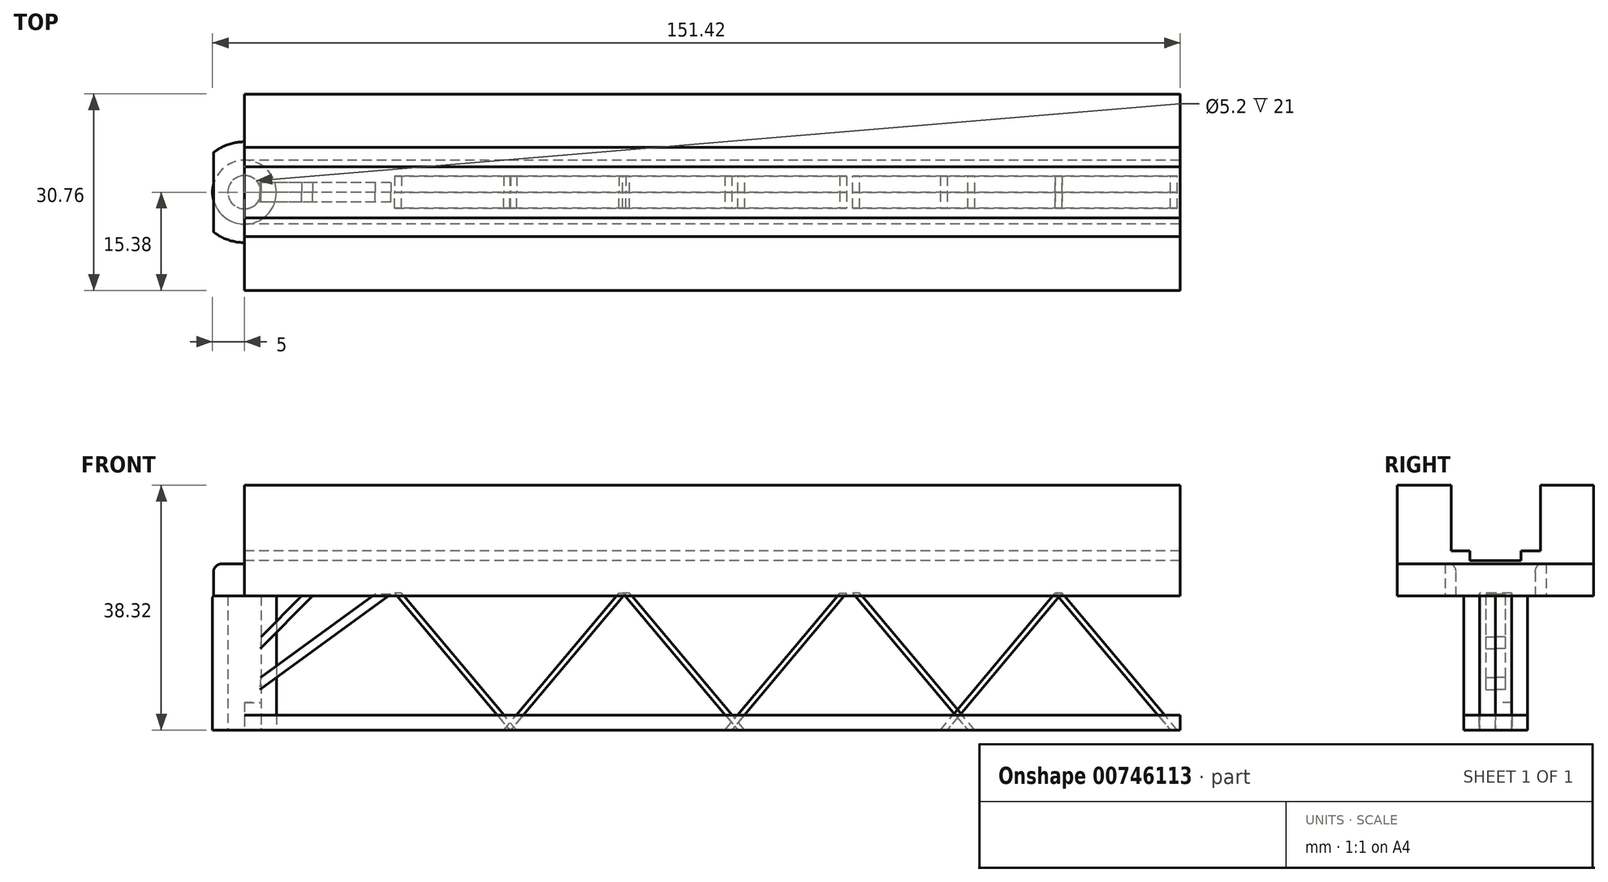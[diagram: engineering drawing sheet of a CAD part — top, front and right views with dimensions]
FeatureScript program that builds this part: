
annotation { "Feature Type Name" : "Feature", "Feature Type Description" : "" }
export const myFeature = defineFeature(function(context is Context, id is Id, definition is map)
    precondition{}
    {
        {
            var Q0;
            Q0=qCreatedBy(makeId("Top.planeOp"),FACE);
            var sketch = newSketch(context, id + "F0", { "sketchPlane" : qUnion([Q0])});
            skCircle(sketch, "E0", {"center": v(0, 0) * mm, "radius": 2.6 * mm});
            skSolve(sketch);
        }
        {
            var Q0;
            Q0=qCreatedBy(makeId("Top.planeOp"),FACE);
            var sketch = newSketch(context, id + "F1", { "sketchPlane" : qUnion([Q0])});
            skCircle(sketch, "E1", {"center": v(0, 0) * mm, "radius": 5 * mm});
            skSolve(sketch);
        }
        {
            var Q0;
            Q0=makeQuery(id+"F1.imprint","IMPRINT",FACE,{"disambiguationData":[TD([[makeQuery(id+"F1.imprint","IMPRINT",EDGE,{"derivedFrom":sQuery(id+"F1.wireOp",EDGE,"E1")}),1.0]])]});
            extrude(context, id + "F2", {"entities" : qUnion([Q0]), "depth" : 21 * mm, "offsetDistance" : 25.4 * mm});
        }
        {
            var Q0;
            Q0=makeQuery(id+"F0.imprint","IMPRINT",FACE,{"disambiguationData":[TD([[makeQuery(id+"F0.imprint","IMPRINT",EDGE,{"derivedFrom":sQuery(id+"F0.wireOp",EDGE,"E0")}),1.0]])]});
            extrude(context, id + "F3", {"entities" : qUnion([Q0]), "operationType" : NewBodyOperationType.REMOVE, "depth" : 22.53 * mm, "offsetDistance" : 25.4 * mm});
        }
        {
            var Q0;
            Q0=qCreatedBy(makeId("Front.planeOp"),FACE);
            var sketch = newSketch(context, id + "F4", { "sketchPlane" : qUnion([Q0])});
            skLineSegment(sketch, "E2", {"start": v(-4.85, 21) * mm, "end": v(-4.85, 24.75) * mm});
            skLineSegment(sketch, "E3", {"start": v(-3.58, 26.02) * mm, "end": v(146.42, 26.02) * mm});
            skLineSegment(sketch, "E4", {"start": v(146.42, 26.02) * mm, "end": v(146.42, 21) * mm});
            skLineSegment(sketch, "E5", {"start": v(146.42, 21) * mm, "end": v(3, 21) * mm});
            skPoint(sketch, "E6.visualSharp", {"position": v(-4.85, 26.02) * mm});
            skArc(sketch, "E6.filletArc", {"start": v(-3.58, 26.02) * mm, "mid": v(-4.48, 25.65) * mm, "end": v(-4.85, 24.75) * mm});
            skLineSegment(sketch, "E7", {"start": v(3, 21) * mm, "end": v(-4.85, 21) * mm});
            skSolve(sketch);
        }
        {
            var Q0;
            Q0=makeQuery(id+"F4.imprint","IMPRINT",FACE,{"disambiguationData":[TD([[makeQuery(id+"F4.imprint","IMPRINT",EDGE,{"derivedFrom":sQuery(id+"F4.wireOp",EDGE,"E2")}),-1.0]])]});
            extrude(context, id + "F5", {"entities" : qUnion([Q0]), "depth" : 22.86 * mm, "offsetDistance" : 25.4 * mm});
        }
        {
            var Q0;
            Q0=makeQuery(id+"F5.opExtrude","CAP_FACE",FACE,{"disambiguationData":[OSD([sQuery(id+"F4.wireOp",EDGE,"E2"),sQuery(id+"F4.wireOp",EDGE,"E3"),sQuery(id+"F4.wireOp",EDGE,"E4"),sQuery(id+"F4.wireOp",EDGE,"E5"),sQuery(id+"F4.wireOp",EDGE,"E6.filletArc"),sQuery(id+"F4.wireOp",EDGE,"E7")])],"isStart":true});
            extrude(context, id + "F6", {"entities" : qUnion([Q0]), "operationType" : NewBodyOperationType.ADD, "depth" : 22.86 * mm, "offsetDistance" : 25.4 * mm});
        }
        {
            var Q0;
            {var subQ0=sQuery(id+"F4.wireOp",EDGE,"E3");Q0=makeQuery(id+"F6.boolean.opBoolean","MERGE",FACE,{"derivedFrom":[makeQuery(id+"F5.opExtrude","SWEPT_FACE",FACE,{"disambiguationData":[OSD([subQ0])]}),makeQuery(id+"F6.opExtrude","SWEPT_FACE",FACE,{"disambiguationData":[OSD([subQ0])]})]});}
            var sketch = newSketch(context, id + "F7", { "sketchPlane" : qUnion([Q0])});
            skLineSegment(sketch, "E8.bottom", {"start": v(73.66, -10.5) * mm, "end": v(94.66, -10.5) * mm});
            skLineSegment(sketch, "E8.top", {"start": v(73.66, 10.5) * mm, "end": v(94.66, 10.5) * mm});
            skLineSegment(sketch, "E8.left", {"start": v(73.66, -10.5) * mm, "end": v(73.66, 10.5) * mm});
            skLineSegment(sketch, "E8.right", {"start": v(94.66, -10.5) * mm, "end": v(94.66, 10.5) * mm});
            skPoint(sketch, "E8.middle", {"position": v(84.16, 0) * mm});
            skSolve(sketch);
        }
        {
            var Q0;
            {var subQ0=sQuery(id+"F4.wireOp",EDGE,"E7");var subQ1=sQuery(id+"F4.wireOp",EDGE,"E5");Q0=makeQuery(id+"F6.boolean.opBoolean","MERGE",FACE,{"derivedFrom":[makeQuery(id+"F5.opExtrude","SWEPT_FACE",FACE,{"disambiguationData":[OSD([subQ1,subQ0])]}),makeQuery(id+"F6.opExtrude","SWEPT_FACE",FACE,{"disambiguationData":[OSD([subQ1,subQ0])]})]});}
            var sketch = newSketch(context, id + "F8", { "sketchPlane" : qUnion([Q0])});
            skLineSegment(sketch, "E9", {"start": v(-4.85, -22.86) * mm, "end": v(-4.85, 22.86) * mm});
            skArc(sketch, "E10", {"start": v(0, 7.9) * mm, "mid": v(-7.9, 0) * mm, "end": v(0, -7.9) * mm});
            skLineSegment(sketch, "E11", {"start": v(0, -22.86) * mm, "end": v(0, -7.9) * mm});
            skLineSegment(sketch, "E12", {"start": v(-4.85, 22.86) * mm, "end": v(0, 22.86) * mm});
            skLineSegment(sketch, "E13", {"start": v(0, 22.86) * mm, "end": v(0, 7.9) * mm});
            skLineSegment(sketch, "E14", {"start": v(-4.85, -22.86) * mm, "end": v(0, -22.86) * mm});
            skLineSegment(sketch, "E15", {"start": v(10.56, -22.86) * mm, "end": v(10.56, 22.86) * mm});
            skSolve(sketch);
        }
        {
            var Q0;
            Q0=qSketchRegion(id+"F8",true);
            extrude(context, id + "F9", {"entities" : qUnion([Q0]), "operationType" : NewBodyOperationType.REMOVE, "oppositeDirection" : true, "depth" : 25.4 * mm, "offsetDistance" : 25.4 * mm});
        }
        {
            var Q0;
            Q0=makeQuery(id+"FSWrnr269RCgbZk_2.boolean.opBoolean","SPLIT",EDGE,{"derivedFrom":makeQuery(id+"F2.opExtrude","CAP_EDGE",EDGE,{"disambiguationData":[OSD([sQuery(id+"F1.wireOp",EDGE,"E1")])],"isStart":false})});
            fillet(context, id + "F10", {"entities" : qUnion([Q0]), "radius" : 0.3 * mm, "tangentPropagation" : true, "allowEdgeOverflow" : false});
        }
        {
            var Q0;
            Q0=qCreatedBy(makeId("Front.planeOp"),FACE);
            var sketch = newSketch(context, id + "F11", { "sketchPlane" : qUnion([Q0])});
            skLineSegment(sketch, "E16", {"start": v(10.69, 21.02) * mm, "end": v(2.5, 12.74) * mm});
            skLineSegment(sketch, "E17", {"start": v(10.69, 21.02) * mm, "end": v(8.95, 21.02) * mm});
            skLineSegment(sketch, "E18", {"start": v(8.95, 21.02) * mm, "end": v(2.59, 14.59) * mm});
            skLineSegment(sketch, "E19", {"start": v(2.59, 14.59) * mm, "end": v(2.5, 12.74) * mm});
            skSolve(sketch);
        }
        {
            var Q0;
            Q0=makeQuery(id+"F11.imprint","IMPRINT",FACE,{"disambiguationData":[TD([[makeQuery(id+"F11.imprint","IMPRINT",EDGE,{"derivedFrom":sQuery(id+"F11.wireOp",EDGE,"E16")}),-1.0]])]});
            extrude(context, id + "F12", {"entities" : qUnion([Q0]), "depth" : 1.52 * mm, "offsetDistance" : 25.4 * mm});
        }
        {
            var Q0;
            Q0=makeQuery(id+"F12.opExtrude","CAP_FACE",FACE,{"disambiguationData":[OSD([sQuery(id+"F11.wireOp",EDGE,"E16"),sQuery(id+"F11.wireOp",EDGE,"E17"),sQuery(id+"F11.wireOp",EDGE,"E18"),sQuery(id+"F11.wireOp",EDGE,"E19")])],"isStart":true});
            extrude(context, id + "F13", {"entities" : qUnion([Q0]), "depth" : 1.52 * mm, "offsetDistance" : 25.4 * mm});
        }
        {
            var Q0;
            Q0=qSketchRegion(id+"F7",true);
            extrude(context, id + "F14", {"entities" : qUnion([Q0]), "operationType" : NewBodyOperationType.REMOVE, "depth" : 12.95 * mm, "offsetDistance" : 25.4 * mm});
        }
        {
            var Q0;
            Q0=qCreatedBy(makeId("Front.planeOp"),FACE);
            var sketch = newSketch(context, id + "F15", { "sketchPlane" : qUnion([Q0])});
            skLineSegment(sketch, "E20", {"start": v(22.9, 21.28) * mm, "end": v(2.41, 6.35) * mm});
            skLineSegment(sketch, "E21", {"start": v(22.9, 21.28) * mm, "end": v(20.45, 21.28) * mm});
            skLineSegment(sketch, "E22", {"start": v(20.45, 21.28) * mm, "end": v(2.5, 8.2) * mm});
            skLineSegment(sketch, "E23", {"start": v(2.5, 8.2) * mm, "end": v(2.41, 6.35) * mm});
            skSolve(sketch);
        }
        {
            var Q0;
            Q0=makeQuery(id+"F15.imprint","IMPRINT",FACE,{"disambiguationData":[TD([[makeQuery(id+"F15.imprint","IMPRINT",EDGE,{"derivedFrom":sQuery(id+"F15.wireOp",EDGE,"E20")}),-1.0]])]});
            extrude(context, id + "F16", {"entities" : qUnion([Q0]), "depth" : 1.52 * mm, "offsetDistance" : 25.4 * mm});
        }
        {
            var Q0;
            Q0=qSketchRegion(id+"F15",true);
            extrude(context, id + "F17", {"entities" : qUnion([Q0]), "oppositeDirection" : true, "depth" : 1.52 * mm, "offsetDistance" : 25.4 * mm});
        }
        {
            var Q0;
            {var subQ0=sQuery(id+"F4.wireOp",EDGE,"E3");Q0=makeQuery(id+"F6.boolean.opBoolean","MERGE",FACE,{"derivedFrom":[makeQuery(id+"F5.opExtrude","SWEPT_FACE",FACE,{"disambiguationData":[OSD([subQ0])]}),makeQuery(id+"F6.opExtrude","SWEPT_FACE",FACE,{"disambiguationData":[OSD([subQ0])]})]});}
            var sketch = newSketch(context, id + "F18", { "sketchPlane" : qUnion([Q0])});
            skLineSegment(sketch, "E24", {"start": v(0, 15.38) * mm, "end": v(146.42, 15.38) * mm});
            skLineSegment(sketch, "E25", {"start": v(146.42, 15.38) * mm, "end": v(146.42, 22.86) * mm});
            skLineSegment(sketch, "E26", {"start": v(146.42, 22.86) * mm, "end": v(0, 22.86) * mm});
            skLineSegment(sketch, "E27", {"start": v(0, 22.86) * mm, "end": v(0, 15.38) * mm});
            skLineSegment(sketch, "E28", {"start": v(0, -15.38) * mm, "end": v(146.42, -15.38) * mm});
            skLineSegment(sketch, "E29", {"start": v(0, -15.38) * mm, "end": v(0, -22.86) * mm});
            skLineSegment(sketch, "E30", {"start": v(0, -22.86) * mm, "end": v(146.42, -22.86) * mm});
            skLineSegment(sketch, "E31", {"start": v(146.42, -22.86) * mm, "end": v(146.42, -15.38) * mm});
            skSolve(sketch);
        }
        {
            var Q0;
            Q0=qSketchRegion(id+"F18",true);
            extrude(context, id + "F19", {"entities" : qUnion([Q0]), "operationType" : NewBodyOperationType.REMOVE, "oppositeDirection" : true, "depth" : 25.4 * mm, "offsetDistance" : 25.4 * mm});
        }
        {
            var Q0;
            Q0=qCreatedBy(makeId("Right.planeOp"),FACE);
            var sketch = newSketch(context, id + "F20", { "sketchPlane" : qUnion([Q0])});
            skLineSegment(sketch, "E32.bottom", {"start": v(-5, 2.35) * mm, "end": v(4.99, 2.35) * mm});
            skLineSegment(sketch, "E32.top", {"start": v(-5, 0) * mm, "end": v(4.99, 0) * mm});
            skLineSegment(sketch, "E32.left", {"start": v(-5, 2.35) * mm, "end": v(-5, 0) * mm});
            skLineSegment(sketch, "E32.right", {"start": v(4.99, 2.35) * mm, "end": v(4.99, 0) * mm});
            skSolve(sketch);
        }
        {
            var Q0;
            Q0=qSketchRegion(id+"F20",true);
            extrude(context, id + "F21", {"entities" : qUnion([Q0]), "depth" : 146.42 * mm, "offsetDistance" : 25.4 * mm});
        }
        {
            var Q0;
            Q0=makeQuery(id+"F21.opExtrude","SWEPT_FACE",FACE,{"disambiguationData":[OSD([sQuery(id+"F20.wireOp",EDGE,"E32.top")])]});
            var sketch = newSketch(context, id + "F22", { "sketchPlane" : qUnion([Q0])});
            skArc(sketch, "E33", {"start": v(0, -2.62) * mm, "mid": v(2.6, 0) * mm, "end": v(0, 2.6) * mm});
            skLineSegment(sketch, "E34", {"start": v(0, 2.6) * mm, "end": v(0, -2.62) * mm});
            skSolve(sketch);
        }
        {
            var Q0;
            Q0=qSketchRegion(id+"F22",true);
            extrude(context, id + "F23", {"entities" : qUnion([Q0]), "operationType" : NewBodyOperationType.REMOVE, "oppositeDirection" : true, "depth" : 4.32 * mm, "offsetDistance" : 25 * mm});
        }
        {
            var Q0;
            Q0=qCreatedBy(makeId("Front.planeOp"),FACE);
            var sketch = newSketch(context, id + "F24", { "sketchPlane" : qUnion([Q0])});
            skLineSegment(sketch, "E35", {"start": v(23.5, 21.45) * mm, "end": v(41.5, 0) * mm});
            skLineSegment(sketch, "E36", {"start": v(41.5, 0) * mm, "end": v(42.58, 0) * mm});
            skLineSegment(sketch, "E37", {"start": v(42.58, 0) * mm, "end": v(24.57, 21.45) * mm});
            skLineSegment(sketch, "E38", {"start": v(24.57, 21.45) * mm, "end": v(23.5, 21.45) * mm});
            skSolve(sketch);
        }
        {
            var Q0;
            Q0=makeQuery(id+"F24.imprint","IMPRINT",FACE,{"disambiguationData":[TD([[makeQuery(id+"F24.imprint","IMPRINT",EDGE,{"derivedFrom":sQuery(id+"F24.wireOp",EDGE,"E35")}),1.0]])]});
            extrude(context, id + "F25", {"entities" : qUnion([Q0]), "depth" : 2.5 * mm, "offsetDistance" : 25 * mm});
        }
        {
            var Q0;
            Q0=qSketchRegion(id+"F24",true);
            extrude(context, id + "F26", {"entities" : qUnion([Q0]), "oppositeDirection" : true, "depth" : 2.5 * mm, "offsetDistance" : 25 * mm});
        }
        {
            var Q0;
            Q0=qCreatedBy(makeId("Front.planeOp"),FACE);
            var sketch = newSketch(context, id + "F27", { "sketchPlane" : qUnion([Q0])});
            skLineSegment(sketch, "E39.MirrorCS", {"start": v(41.65, 0) * mm, "end": v(40.57, 0) * mm});
            skLineSegment(sketch, "E40.MirrorCS", {"start": v(58.58, 21.45) * mm, "end": v(59.65, 21.45) * mm});
            skLineSegment(sketch, "E41.MirrorCS", {"start": v(59.65, 21.45) * mm, "end": v(41.65, 0) * mm});
            skLineSegment(sketch, "E42.MirrorCS", {"start": v(40.57, 0) * mm, "end": v(58.58, 21.45) * mm});
            skSolve(sketch);
        }
        {
            var Q0;
            Q0=makeQuery(id+"F27.imprint","IMPRINT",FACE,{"disambiguationData":[TD([[makeQuery(id+"F27.imprint","IMPRINT",EDGE,{"derivedFrom":sQuery(id+"F27.wireOp",EDGE,"E39.MirrorCS")}),-1.0]])]});
            extrude(context, id + "F28", {"entities" : qUnion([Q0]), "depth" : 2.5 * mm, "offsetDistance" : 25 * mm});
        }
        {
            var Q0;
            Q0=qSketchRegion(id+"F27",true);
            extrude(context, id + "F29", {"entities" : qUnion([Q0]), "oppositeDirection" : true, "depth" : 2.5 * mm, "offsetDistance" : 25 * mm});
        }
        {
            var Q0;
            Q0=makeQuery(id+"F25.opExtrude","SWEPT_BODY",BODY,{"disambiguationData":[OSD([sQuery(id+"F24.wireOp",EDGE,"E35"),sQuery(id+"F24.wireOp",EDGE,"E36"),sQuery(id+"F24.wireOp",EDGE,"E37"),sQuery(id+"F24.wireOp",EDGE,"E38")])]});
            transform(context, id + "F30", {"entities" : qUnion([Q0]), "transformType" : TransformType.TRANSLATION_3D, "dx" : 35.7 * mm, "dy" : 0 * mm, "dz" : 0 * mm, "makeCopy" : true});
        }
        {
            var Q0;
            Q0=makeQuery(id+"F30.opPattern","COPY",BODY,{"derivedFrom":makeQuery(id+"F25.opExtrude","SWEPT_BODY",BODY,{"disambiguationData":[OSD([sQuery(id+"F24.wireOp",EDGE,"E35"),sQuery(id+"F24.wireOp",EDGE,"E36"),sQuery(id+"F24.wireOp",EDGE,"E37"),sQuery(id+"F24.wireOp",EDGE,"E38")])]}),"instanceName":"1"});
            transform(context, id + "F31", {"entities" : qUnion([Q0]), "transformType" : TransformType.TRANSLATION_3D, "dx" : 0 * mm, "dy" : 2.5 * mm, "dz" : 0 * mm, "makeCopy" : true});
        }
        {
            var Q0;
            Q0=makeQuery(id+"F29.opExtrude","SWEPT_BODY",BODY,{"disambiguationData":[OSD([sQuery(id+"F27.wireOp",EDGE,"E39.MirrorCS"),sQuery(id+"F27.wireOp",EDGE,"E40.MirrorCS"),sQuery(id+"F27.wireOp",EDGE,"E41.MirrorCS"),sQuery(id+"F27.wireOp",EDGE,"E42.MirrorCS")])]});
            transform(context, id + "F32", {"entities" : qUnion([Q0]), "transformType" : TransformType.TRANSLATION_3D, "dx" : 34.6 * mm, "dy" : 0 * mm, "dz" : 0 * mm, "makeCopy" : true});
        }
        {
            var Q0;
            Q0=makeQuery(id+"F32.opPattern","COPY",BODY,{"derivedFrom":makeQuery(id+"F29.opExtrude","SWEPT_BODY",BODY,{"disambiguationData":[OSD([sQuery(id+"F27.wireOp",EDGE,"E39.MirrorCS"),sQuery(id+"F27.wireOp",EDGE,"E40.MirrorCS"),sQuery(id+"F27.wireOp",EDGE,"E41.MirrorCS"),sQuery(id+"F27.wireOp",EDGE,"E42.MirrorCS")])]}),"instanceName":"1"});
            transform(context, id + "F33", {"entities" : qUnion([Q0]), "transformType" : TransformType.TRANSLATION_3D, "dx" : 0 * mm, "dy" : -2.5 * mm, "dz" : 0 * mm, "makeCopy" : true});
        }
        {
            var Q0;
            Q0=makeQuery(id+"F31.opPattern","COPY",BODY,{"derivedFrom":makeQuery(id+"F30.opPattern","COPY",BODY,{"derivedFrom":makeQuery(id+"F25.opExtrude","SWEPT_BODY",BODY,{"disambiguationData":[OSD([sQuery(id+"F24.wireOp",EDGE,"E35"),sQuery(id+"F24.wireOp",EDGE,"E36"),sQuery(id+"F24.wireOp",EDGE,"E37"),sQuery(id+"F24.wireOp",EDGE,"E38")])]}),"instanceName":"1"}),"instanceName":"1"});
            transform(context, id + "F34", {"entities" : qUnion([Q0]), "transformType" : TransformType.TRANSLATION_3D, "dx" : 36 * mm, "dy" : -2.5 * mm, "dz" : 0 * mm, "makeCopy" : true});
        }
        {
            var Q0;
            Q0=makeQuery(id+"F34.opPattern","COPY",BODY,{"derivedFrom":makeQuery(id+"F31.opPattern","COPY",BODY,{"derivedFrom":makeQuery(id+"F30.opPattern","COPY",BODY,{"derivedFrom":makeQuery(id+"F25.opExtrude","SWEPT_BODY",BODY,{"disambiguationData":[OSD([sQuery(id+"F24.wireOp",EDGE,"E35"),sQuery(id+"F24.wireOp",EDGE,"E36"),sQuery(id+"F24.wireOp",EDGE,"E37"),sQuery(id+"F24.wireOp",EDGE,"E38")])]}),"instanceName":"1"}),"instanceName":"1"}),"instanceName":"1"});
            transform(context, id + "F35", {"entities" : qUnion([Q0]), "transformType" : TransformType.TRANSLATION_3D, "dx" : 0 * mm, "dy" : 2.5 * mm, "dz" : 0 * mm, "makeCopy" : true});
        }
        {
            var Q0;
            Q0=makeQuery(id+"F32.opPattern","COPY",BODY,{"derivedFrom":makeQuery(id+"F29.opExtrude","SWEPT_BODY",BODY,{"disambiguationData":[OSD([sQuery(id+"F27.wireOp",EDGE,"E39.MirrorCS"),sQuery(id+"F27.wireOp",EDGE,"E40.MirrorCS"),sQuery(id+"F27.wireOp",EDGE,"E41.MirrorCS"),sQuery(id+"F27.wireOp",EDGE,"E42.MirrorCS")])]}),"instanceName":"1"});
            transform(context, id + "F36", {"entities" : qUnion([Q0]), "transformType" : TransformType.TRANSLATION_3D, "dx" : 33.7 * mm, "dy" : 0 * mm, "dz" : 0 * mm, "makeCopy" : true});
        }
        {
            var Q0;
            Q0=makeQuery(id+"F36.opPattern","COPY",BODY,{"derivedFrom":makeQuery(id+"F32.opPattern","COPY",BODY,{"derivedFrom":makeQuery(id+"F29.opExtrude","SWEPT_BODY",BODY,{"disambiguationData":[OSD([sQuery(id+"F27.wireOp",EDGE,"E39.MirrorCS"),sQuery(id+"F27.wireOp",EDGE,"E40.MirrorCS"),sQuery(id+"F27.wireOp",EDGE,"E41.MirrorCS"),sQuery(id+"F27.wireOp",EDGE,"E42.MirrorCS")])]}),"instanceName":"1"}),"instanceName":"1"});
            transform(context, id + "F37", {"entities" : qUnion([Q0]), "transformType" : TransformType.TRANSLATION_3D, "dx" : 0 * mm, "dy" : -2.5 * mm, "dz" : 0 * mm, "makeCopy" : true});
        }
        {
            var Q0;
            Q0=makeQuery(id+"F35.opPattern","COPY",BODY,{"derivedFrom":makeQuery(id+"F34.opPattern","COPY",BODY,{"derivedFrom":makeQuery(id+"F31.opPattern","COPY",BODY,{"derivedFrom":makeQuery(id+"F30.opPattern","COPY",BODY,{"derivedFrom":makeQuery(id+"F25.opExtrude","SWEPT_BODY",BODY,{"disambiguationData":[OSD([sQuery(id+"F24.wireOp",EDGE,"E35"),sQuery(id+"F24.wireOp",EDGE,"E36"),sQuery(id+"F24.wireOp",EDGE,"E37"),sQuery(id+"F24.wireOp",EDGE,"E38")])]}),"instanceName":"1"}),"instanceName":"1"}),"instanceName":"1"}),"instanceName":"1"});
            transform(context, id + "F38", {"entities" : qUnion([Q0]), "transformType" : TransformType.TRANSLATION_3D, "dx" : 31.7 * mm, "dy" : 0 * mm, "dz" : 0 * mm, "makeCopy" : true});
        }
        {
            var Q0;
            Q0=makeQuery(id+"F38.opPattern","COPY",BODY,{"derivedFrom":makeQuery(id+"F35.opPattern","COPY",BODY,{"derivedFrom":makeQuery(id+"F34.opPattern","COPY",BODY,{"derivedFrom":makeQuery(id+"F31.opPattern","COPY",BODY,{"derivedFrom":makeQuery(id+"F30.opPattern","COPY",BODY,{"derivedFrom":makeQuery(id+"F25.opExtrude","SWEPT_BODY",BODY,{"disambiguationData":[OSD([sQuery(id+"F24.wireOp",EDGE,"E35"),sQuery(id+"F24.wireOp",EDGE,"E36"),sQuery(id+"F24.wireOp",EDGE,"E37"),sQuery(id+"F24.wireOp",EDGE,"E38")])]}),"instanceName":"1"}),"instanceName":"1"}),"instanceName":"1"}),"instanceName":"1"}),"instanceName":"1"});
            transform(context, id + "F39", {"entities" : qUnion([Q0]), "transformType" : TransformType.TRANSLATION_3D, "dx" : 0 * mm, "dy" : -2.5 * mm, "dz" : 0 * mm, "makeCopy" : true});
        }
        {
            var Q0;
            Q0=qCreatedBy(makeId("Right.planeOp"),FACE);
            var sketch = newSketch(context, id + "F40", { "sketchPlane" : qUnion([Q0])});
            skLineSegment(sketch, "E43", {"start": v(15.38, 26.02) * mm, "end": v(15.38, 38.32) * mm});
            skLineSegment(sketch, "E44", {"start": v(15.38, 38.32) * mm, "end": v(-15.38, 38.32) * mm});
            skLineSegment(sketch, "E45", {"start": v(-15.38, 38.32) * mm, "end": v(-15.38, 26.02) * mm});
            skLineSegment(sketch, "E46", {"start": v(-15.38, 26.02) * mm, "end": v(15.38, 26.02) * mm});
            skSolve(sketch);
        }
        {
            var Q0;
            Q0=makeQuery(id+"F40.imprint","IMPRINT",FACE,{"disambiguationData":[TD([[makeQuery(id+"F40.imprint","IMPRINT",EDGE,{"derivedFrom":sQuery(id+"F40.wireOp",EDGE,"E43")}),1.0]])]});
            var sketch = newSketch(context, id + "F41", { "sketchPlane" : qUnion([Q0])});
            skLineSegment(sketch, "E47", {"start": v(0.05, 28.04) * mm, "end": v(-6.95, 28.04) * mm});
            skLineSegment(sketch, "E48", {"start": v(0.05, 28.04) * mm, "end": v(7.05, 28.04) * mm});
            skLineSegment(sketch, "E49", {"start": v(-6.95, 28.04) * mm, "end": v(-6.95, 38.44) * mm});
            skLineSegment(sketch, "E50", {"start": v(7.05, 28.04) * mm, "end": v(7.05, 38.44) * mm});
            skLineSegment(sketch, "E51", {"start": v(7.05, 38.44) * mm, "end": v(-6.95, 38.44) * mm});
            skSolve(sketch);
        }
        {
            var Q0;
            Q0 = qSketchRegion(id + "F40", true);
            extrude(context, id + "F42", {"entities" : qUnion([Q0]), "operationType" : NewBodyOperationType.ADD, "depth" : 146.4 * mm, "offsetDistance" : 25 * mm});
        }
        {
            var Q0;
            {var subQ5=sQuery(id+"F41.wireOp",EDGE,"E47");Q0=makeQuery(id+"F41.imprint","IMPRINT",FACE,{"disambiguationData":[TD([[makeQuery(id+"F41.imprint","IMPRINT",EDGE,{"derivedFrom":subQ5}),-1.0]])]});}
            extrude(context, id + "F43", {"entities" : qUnion([Q0]), "operationType" : NewBodyOperationType.REMOVE, "depth" : 148.9 * mm, "offsetDistance" : 25 * mm});
        }
        {
            var Q0;
            Q0=qCreatedBy(makeId("Right.planeOp"),FACE);
            var sketch = newSketch(context, id + "F44", { "sketchPlane" : qUnion([Q0])});
            skLineSegment(sketch, "E52", {"start": v(0, 28.04) * mm, "end": v(-4, 28.04) * mm});
            skLineSegment(sketch, "E53", {"start": v(-4, 28.04) * mm, "end": v(-4, 26.54) * mm});
            skLineSegment(sketch, "E54", {"start": v(-4, 26.54) * mm, "end": v(0.04, 26.54) * mm});
            skLineSegment(sketch, "E55", {"start": v(0.04, 26.54) * mm, "end": v(4, 26.54) * mm});
            skLineSegment(sketch, "E56", {"start": v(0, 28.04) * mm, "end": v(4, 28.04) * mm});
            skLineSegment(sketch, "E57", {"start": v(4, 28.04) * mm, "end": v(4, 26.54) * mm});
            skSolve(sketch);
        }
        {
            var Q0;
            Q0=makeQuery(id+"F44.imprint","IMPRINT",FACE,{"disambiguationData":[TD([[makeQuery(id+"F44.imprint","IMPRINT",EDGE,{"derivedFrom":sQuery(id+"F44.wireOp",EDGE,"E52")}),1.0]])]});
            extrude(context, id + "F45", {"entities" : qUnion([Q0]), "operationType" : NewBodyOperationType.REMOVE, "depth" : 214 * mm, "offsetDistance" : 25 * mm});
        }
    });
